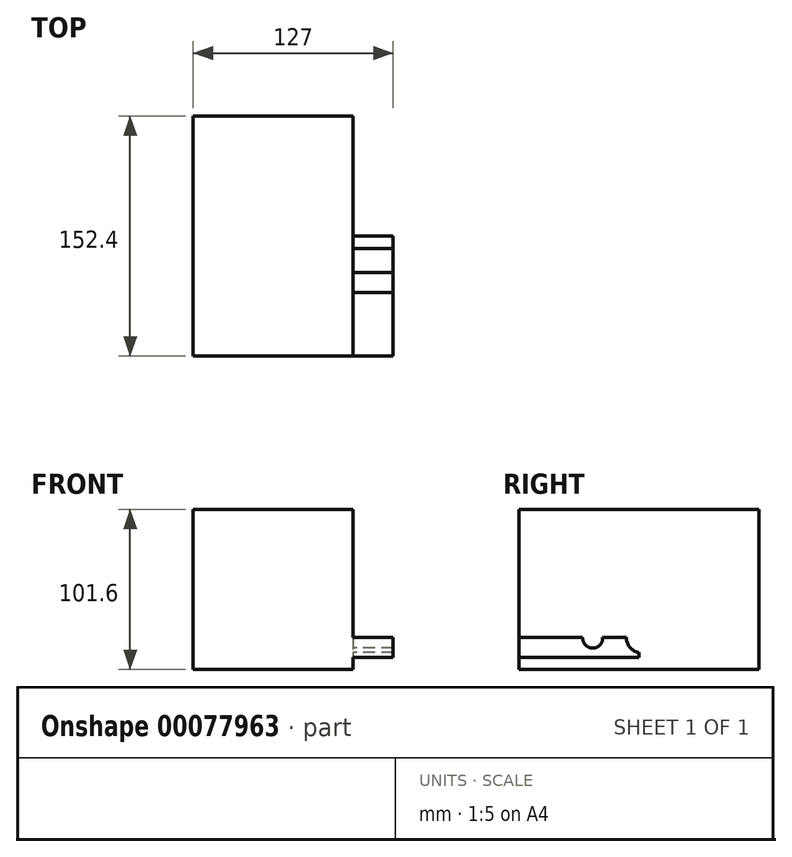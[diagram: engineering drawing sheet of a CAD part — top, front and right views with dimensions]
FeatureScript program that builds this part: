
annotation { "Feature Type Name" : "Feature", "Feature Type Description" : "" }
export const myFeature = defineFeature(function(context is Context, id is Id, definition is map)
    precondition{}
    {
        {
            var Q0;
            Q0=qCreatedBy(makeId("Top.planeOp"),FACE);
            var sketch = newSketch(context, id + "F0", { "sketchPlane" : qUnion([Q0])});
            skLineSegment(sketch, "E0.bottom", {"start": v(-41.95, 74.87) * mm, "end": v(59.65, 74.87) * mm});
            skLineSegment(sketch, "E0.top", {"start": v(-41.95, -77.53) * mm, "end": v(59.65, -77.53) * mm});
            skLineSegment(sketch, "E0.left", {"start": v(-41.95, 74.87) * mm, "end": v(-41.95, -77.53) * mm});
            skLineSegment(sketch, "E0.right", {"start": v(59.65, 74.87) * mm, "end": v(59.65, -77.53) * mm});
            skSolve(sketch);
        }
        {
            var Q0;
            Q0=makeQuery(id+"F0.imprint","IMPRINT",FACE,{"disambiguationData":[TD([[makeQuery(id+"F0.imprint","IMPRINT",EDGE,{"derivedFrom":sQuery(id+"F0.wireOp",EDGE,"E0.bottom")}),-1.0]])]});
            extrude(context, id + "F1", {"entities" : qUnion([Q0]), "depth" : 101.6 * mm});
        }
        {
            var Q0;
            Q0=makeQuery(id+"F1.opExtrude","SWEPT_FACE",FACE,{"disambiguationData":[OSD([sQuery(id+"F0.wireOp",EDGE,"E0.right")])]});
            var sketch = newSketch(context, id + "F2", { "sketchPlane" : qUnion([Q0])});
            skCircle(sketch, "E1", {"center": v(-30.8, 19.9) * mm, "radius": 6.35 * mm});
            skCircle(sketch, "E2", {"center": v(0, 19.9) * mm, "radius": 9.29 * mm});
            skLineSegment(sketch, "E3", {"start": v(-77.53, 20.33) * mm, "end": v(74.87, 20.33) * mm});
            skLineSegment(sketch, "E4", {"start": v(-1.33, 20.33) * mm, "end": v(-1.33, 0) * mm});
            skLineSegment(sketch, "E5.bottom", {"start": v(74.87, 33.03) * mm, "end": v(-77.53, 33.03) * mm});
            skLineSegment(sketch, "E5.top", {"start": v(74.87, 7.63) * mm, "end": v(-77.53, 7.63) * mm});
            skLineSegment(sketch, "E5.left", {"start": v(74.87, 33.03) * mm, "end": v(74.87, 7.63) * mm});
            skLineSegment(sketch, "E5.right", {"start": v(-77.53, 33.03) * mm, "end": v(-77.53, 7.63) * mm});
            skPoint(sketch, "E5.middle", {"position": v(-1.33, 20.33) * mm});
            skSolve(sketch);
        }
        {
            var Q0;
            {var subQ1=sQuery(id+"F2.wireOp",EDGE,"E3");var subQ3=sQuery(id+"F2.wireOp",EDGE,"E1");var subQ9=makeQuery(id+"F2.imprint","INTERSECT",VERTEX,{"disambiguationData":[OD(0.0)],"derivedFrom":[subQ3,subQ1]});Q0=makeQuery(id+"F2.imprint","IMPRINT",FACE,{"disambiguationData":[TD([[makeQuery(id+"F2.imprint","IMPRINT",EDGE,{"disambiguationData":[TD([[subQ9,-1.0]])],"derivedFrom":subQ3}),-1.0]])]});}
            extrude(context, id + "F3", {"entities" : qUnion([Q0]), "operationType" : NewBodyOperationType.ADD, "depth" : 25.4 * mm});
        }
    });
